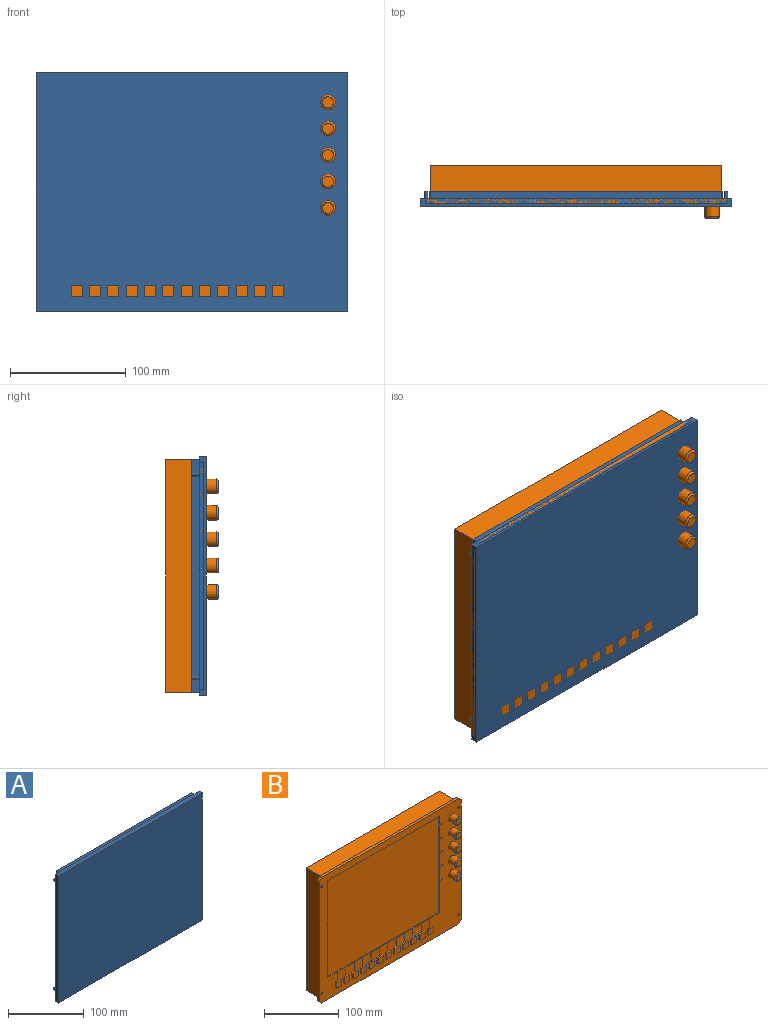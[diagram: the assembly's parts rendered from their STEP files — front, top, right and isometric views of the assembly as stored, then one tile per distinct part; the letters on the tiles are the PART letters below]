
ASSEMBLY  parts=2 mates=1
PART A: 19 faces, bbox 269.5x12.7x206 mm
  f0: plane 269.5x206mm, normal (0,1,0), area 4277.8mm2, adj f1,f2,f3,f4,f6,f7,f8,f9
  f1: plane 206x6.35mm, normal (1,0,0), area 1308.1mm2, adj f0,f2,f4,f5
  f2: plane 269.5x6.35mm, normal (0,0,1), area 1711.3mm2, adj f0,f1,f3,f5
  f3: plane 206x6.35mm, normal (-1,0,0), area 1308.1mm2, adj f0,f2,f4,f5
  f4: plane 269.5x6.35mm, normal (0,0,-1), area 1711.3mm2, adj f0,f1,f3,f5
  f5: plane 269.5x206mm, normal (0,-1,0), area 55517mm2, adj f1,f2,f3,f4
  f6: plane 253.5x6.35mm, normal (0,0,1), area 1609.7mm2, adj f0,f7,f9,f10
  f7: plane 202x6.35mm, normal (-1,0,0), area 1282.7mm2, adj f0,f6,f8,f10
  f8: plane 253.5x6.35mm, normal (0,0,-1), area 1609.7mm2, adj f0,f7,f9,f10
  f9: plane 202x6.35mm, normal (1,0,0), area 1282.7mm2, adj f0,f6,f8,f10
  f10: plane 253.5x202mm, normal (0,1,0), area 51207mm2, adj f6,f7,f8,f9
  f11: cylinder r=1.6mm len=6.35mm, axis (0,-1,0), area 63.8mm2, adj f0,f12
  f12: plane 3.2x3.2mm, normal (0,1,0), area 8mm2, adj f11
  f13: cylinder r=1.6mm len=6.35mm, axis (0,-1,0), area 63.8mm2, adj f0,f14
  f14: plane 3.2x3.2mm, normal (0,1,0), area 8mm2, adj f13
  f15: cylinder r=1.6mm len=6.35mm, axis (0,-1,0), area 63.8mm2, adj f0,f16
  f16: plane 3.2x3.2mm, normal (0,1,0), area 8mm2, adj f15
  f17: cylinder r=1.6mm len=6.35mm, axis (0,-1,0), area 63.8mm2, adj f0,f18
  f18: plane 3.2x3.2mm, normal (0,1,0), area 8mm2, adj f17
PART B: 219 faces, bbox 269.5x45.7x206 mm
  f0: plane 14.54x0.51mm, normal (1,0,0), area 7.4mm2, adj f2,f5,f88,f89
  f1: plane 14.54x0.51mm, normal (-1,0,0), area 7.4mm2, adj f2,f5,f88,f89
  f2: plane 14.54x0.25mm, normal (0,-1,0), area 3.7mm2, adj f0,f1,f5,f88
  f3: plane 9.53x2.54mm, normal (0,0,-1), area 24.2mm2, adj f4,f6,f7,f89
  f4: plane 9.53x2.54mm, normal (1,0,0), area 24.2mm2, adj f3,f5,f7,f89
  f5: plane 9.53x3.05mm, normal (0,0,1), area 24.3mm2, adj f0,f1,f2,f4,f6,f7,f89
  f6: plane 9.53x2.54mm, normal (-1,0,0), area 24.2mm2, adj f3,f5,f7,f89
  f7: plane 9.53x9.53mm, normal (0,-1,0), area 90.7mm2, adj f3,f4,f5,f6
  f8: plane 14.54x0.51mm, normal (1,0,0), area 7.4mm2, adj f10,f13,f88,f89
  f9: plane 14.54x0.51mm, normal (-1,0,0), area 7.4mm2, adj f10,f13,f88,f89
  f10: plane 14.54x0.25mm, normal (0,-1,0), area 3.7mm2, adj f8,f9,f13,f88
  f11: plane 9.53x2.54mm, normal (0,0,-1), area 24.2mm2, adj f12,f14,f15,f89
  f12: plane 9.53x2.54mm, normal (1,0,0), area 24.2mm2, adj f11,f13,f15,f89
  f13: plane 9.53x3.05mm, normal (0,0,1), area 24.3mm2, adj f8,f9,f10,f12,f14,f15,f89
  f14: plane 9.53x2.54mm, normal (-1,0,0), area 24.2mm2, adj f11,f13,f15,f89
  f15: plane 9.53x9.53mm, normal (0,-1,0), area 90.7mm2, adj f11,f12,f13,f14
  f16: plane 14.54x0.51mm, normal (1,0,0), area 7.4mm2, adj f18,f21,f88,f89
  f17: plane 14.54x0.51mm, normal (-1,0,0), area 7.4mm2, adj f18,f21,f88,f89
  f18: plane 14.54x0.25mm, normal (0,-1,0), area 3.7mm2, adj f16,f17,f21,f88
  f19: plane 9.53x2.54mm, normal (0,0,-1), area 24.2mm2, adj f20,f22,f23,f89
  f20: plane 9.53x2.54mm, normal (1,0,0), area 24.2mm2, adj f19,f21,f23,f89
  f21: plane 9.53x3.05mm, normal (0,0,1), area 24.3mm2, adj f16,f17,f18,f20,f22,f23,f89
  f22: plane 9.53x2.54mm, normal (-1,0,0), area 24.2mm2, adj f19,f21,f23,f89
  f23: plane 9.53x9.53mm, normal (0,-1,0), area 90.7mm2, adj f19,f20,f21,f22
  f24: plane 14.54x0.51mm, normal (1,0,0), area 7.4mm2, adj f26,f29,f88,f89
  f25: plane 14.54x0.51mm, normal (-1,0,0), area 7.4mm2, adj f26,f29,f88,f89
  f26: plane 14.54x0.25mm, normal (0,-1,0), area 3.7mm2, adj f24,f25,f29,f88
  f27: plane 9.53x2.54mm, normal (0,0,-1), area 24.2mm2, adj f28,f30,f31,f89
  f28: plane 9.53x2.54mm, normal (1,0,0), area 24.2mm2, adj f27,f29,f31,f89
  f29: plane 9.53x3.05mm, normal (0,0,1), area 24.3mm2, adj f24,f25,f26,f28,f30,f31,f89
  f30: plane 9.53x2.54mm, normal (-1,0,0), area 24.2mm2, adj f27,f29,f31,f89
  f31: plane 9.53x9.53mm, normal (0,-1,0), area 90.7mm2, adj f27,f28,f29,f30
  f32: plane 14.54x0.51mm, normal (1,0,0), area 7.4mm2, adj f34,f37,f88,f89
  f33: plane 14.54x0.51mm, normal (-1,0,0), area 7.4mm2, adj f34,f37,f88,f89
  f34: plane 14.54x0.25mm, normal (0,-1,0), area 3.7mm2, adj f32,f33,f37,f88
  f35: plane 9.53x2.54mm, normal (0,0,-1), area 24.2mm2, adj f36,f38,f39,f89
  f36: plane 9.53x2.54mm, normal (1,0,0), area 24.2mm2, adj f35,f37,f39,f89
  f37: plane 9.53x3.05mm, normal (0,0,1), area 24.3mm2, adj f32,f33,f34,f36,f38,f39,f89
  f38: plane 9.53x2.54mm, normal (-1,0,0), area 24.2mm2, adj f35,f37,f39,f89
  f39: plane 9.53x9.53mm, normal (0,-1,0), area 90.7mm2, adj f35,f36,f37,f38
  f40: plane 14.54x0.51mm, normal (1,0,0), area 7.4mm2, adj f42,f45,f88,f89
  f41: plane 14.54x0.51mm, normal (-1,0,0), area 7.4mm2, adj f42,f45,f88,f89
  f42: plane 14.54x0.25mm, normal (0,-1,0), area 3.7mm2, adj f40,f41,f45,f88
  f43: plane 9.53x2.54mm, normal (0,0,-1), area 24.2mm2, adj f44,f46,f47,f89
  f44: plane 9.53x2.54mm, normal (1,0,0), area 24.2mm2, adj f43,f45,f47,f89
  f45: plane 9.53x3.05mm, normal (0,0,1), area 24.3mm2, adj f40,f41,f42,f44,f46,f47,f89
  f46: plane 9.53x2.54mm, normal (-1,0,0), area 24.2mm2, adj f43,f45,f47,f89
  f47: plane 9.53x9.53mm, normal (0,-1,0), area 90.7mm2, adj f43,f44,f45,f46
  f48: plane 14.54x0.51mm, normal (1,0,0), area 7.4mm2, adj f50,f53,f88,f89
  f49: plane 14.54x0.51mm, normal (-1,0,0), area 7.4mm2, adj f50,f53,f88,f89
  f50: plane 14.54x0.25mm, normal (0,-1,0), area 3.7mm2, adj f48,f49,f53,f88
  f51: plane 9.53x2.54mm, normal (0,0,-1), area 24.2mm2, adj f52,f54,f55,f89
  f52: plane 9.53x2.54mm, normal (1,0,0), area 24.2mm2, adj f51,f53,f55,f89
  f53: plane 9.53x3.05mm, normal (0,0,1), area 24.3mm2, adj f48,f49,f50,f52,f54,f55,f89
  f54: plane 9.53x2.54mm, normal (-1,0,0), area 24.2mm2, adj f51,f53,f55,f89
  f55: plane 9.53x9.53mm, normal (0,-1,0), area 90.7mm2, adj f51,f52,f53,f54
  f56: plane 14.54x0.51mm, normal (1,0,0), area 7.4mm2, adj f58,f61,f88,f89
  f57: plane 14.54x0.51mm, normal (-1,0,0), area 7.4mm2, adj f58,f61,f88,f89
  f58: plane 14.54x0.25mm, normal (0,-1,0), area 3.7mm2, adj f56,f57,f61,f88
  f59: plane 9.53x2.54mm, normal (0,0,-1), area 24.2mm2, adj f60,f62,f63,f89
  f60: plane 9.53x2.54mm, normal (1,0,0), area 24.2mm2, adj f59,f61,f63,f89
  f61: plane 9.53x3.05mm, normal (0,0,1), area 24.3mm2, adj f56,f57,f58,f60,f62,f63,f89
  f62: plane 9.53x2.54mm, normal (-1,0,0), area 24.2mm2, adj f59,f61,f63,f89
  f63: plane 9.53x9.53mm, normal (0,-1,0), area 90.7mm2, adj f59,f60,f61,f62
  f64: plane 14.54x0.51mm, normal (1,0,0), area 7.4mm2, adj f66,f69,f88,f89
  f65: plane 14.54x0.51mm, normal (-1,0,0), area 7.4mm2, adj f66,f69,f88,f89
  f66: plane 14.54x0.25mm, normal (0,-1,0), area 3.7mm2, adj f64,f65,f69,f88
  f67: plane 9.53x2.54mm, normal (0,0,-1), area 24.2mm2, adj f68,f70,f71,f89
  f68: plane 9.53x2.54mm, normal (1,0,0), area 24.2mm2, adj f67,f69,f71,f89
  f69: plane 9.53x3.05mm, normal (0,0,1), area 24.3mm2, adj f64,f65,f66,f68,f70,f71,f89
  f70: plane 9.53x2.54mm, normal (-1,0,0), area 24.2mm2, adj f67,f69,f71,f89
  f71: plane 9.53x9.53mm, normal (0,-1,0), area 90.7mm2, adj f67,f68,f69,f70
  f72: plane 14.54x0.51mm, normal (1,0,0), area 7.4mm2, adj f74,f77,f88,f89
  f73: plane 14.54x0.51mm, normal (-1,0,0), area 7.4mm2, adj f74,f77,f88,f89
  f74: plane 14.54x0.25mm, normal (0,-1,0), area 3.7mm2, adj f72,f73,f77,f88
  f75: plane 9.53x2.54mm, normal (0,0,-1), area 24.2mm2, adj f76,f78,f79,f89
  f76: plane 9.53x2.54mm, normal (1,0,0), area 24.2mm2, adj f75,f77,f79,f89
  f77: plane 9.53x3.05mm, normal (0,0,1), area 24.3mm2, adj f72,f73,f74,f76,f78,f79,f89
  f78: plane 9.53x2.54mm, normal (-1,0,0), area 24.2mm2, adj f75,f77,f79,f89
  f79: plane 9.53x9.53mm, normal (0,-1,0), area 90.7mm2, adj f75,f76,f77,f78
  f80: plane 14.54x0.51mm, normal (1,0,0), area 7.4mm2, adj f82,f85,f88,f89
  f81: plane 14.54x0.51mm, normal (-1,0,0), area 7.4mm2, adj f82,f85,f88,f89
  f82: plane 14.54x0.25mm, normal (0,-1,0), area 3.7mm2, adj f80,f81,f85,f88
  f83: plane 9.53x2.54mm, normal (0,0,-1), area 24.2mm2, adj f84,f86,f87,f89
  f84: plane 9.53x2.54mm, normal (1,0,0), area 24.2mm2, adj f83,f85,f87,f89
  f85: plane 9.53x3.05mm, normal (0,0,1), area 24.3mm2, adj f80,f81,f82,f84,f86,f87,f89
  f86: plane 9.53x2.54mm, normal (-1,0,0), area 24.2mm2, adj f83,f85,f87,f89
  f87: plane 9.53x9.53mm, normal (0,-1,0), area 90.7mm2, adj f83,f84,f85,f86
  f88: plane 211.33x1.59mm, normal (0,0,1), area 333.9mm2, adj f0,f1,f2,f8,f9,f10,f16,f17
  f89: plane 269.5x206mm, normal (0,-1,0), area 20165.7mm2, adj f0,f1,f3,f4,f5,f6,f8,f9
  f90: cylinder r=1.59mm len=6.35mm, axis (0,1,0), area 63.3mm2, adj f91,f169
  f91: plane 3.18x3.18mm, normal (0,1,0), area 7.9mm2, adj f90
  f92: cylinder r=1.59mm len=6.35mm, axis (0,1,0), area 63.3mm2, adj f93,f169
  f93: plane 3.18x3.18mm, normal (0,1,0), area 7.9mm2, adj f92
  f94: cylinder r=1.59mm len=6.35mm, axis (0,1,0), area 63.3mm2, adj f95,f169
  f95: plane 3.18x3.18mm, normal (0,1,0), area 7.9mm2, adj f94
  f96: cylinder r=1.59mm len=6.35mm, axis (0,1,0), area 63.3mm2, adj f97,f169
  f97: plane 3.18x3.18mm, normal (0,1,0), area 7.9mm2, adj f96
  f98: cylinder r=1.59mm len=6.35mm, axis (0,1,0), area 63.3mm2, adj f99,f169
  f99: plane 3.18x3.18mm, normal (0,1,0), area 7.9mm2, adj f98
  f100: cylinder r=1.59mm len=6.35mm, axis (0,1,0), area 63.3mm2, adj f101,f169
  f101: plane 3.18x3.18mm, normal (0,1,0), area 7.9mm2, adj f100
  f102: cylinder r=1.59mm len=6.35mm, axis (0,1,0), area 63.3mm2, adj f103,f169
  f103: plane 3.18x3.18mm, normal (0,1,0), area 7.9mm2, adj f102
  f104: cylinder r=1.59mm len=6.35mm, axis (0,1,0), area 63.3mm2, adj f105,f169
  f105: plane 3.18x3.18mm, normal (0,1,0), area 7.9mm2, adj f104
  f106: cylinder r=1.59mm len=6.35mm, axis (0,1,0), area 63.3mm2, adj f107,f169
  f107: plane 3.18x3.18mm, normal (0,1,0), area 7.9mm2, adj f106
  f108: cylinder r=1.59mm len=6.35mm, axis (0,1,0), area 63.3mm2, adj f109,f169
  f109: plane 3.18x3.18mm, normal (0,1,0), area 7.9mm2, adj f108
  f110: cylinder r=1.59mm len=6.35mm, axis (0,1,0), area 63.3mm2, adj f111,f169
  f111: plane 3.18x3.18mm, normal (0,1,0), area 7.9mm2, adj f110
  f112: cylinder r=1.59mm len=6.35mm, axis (0,1,0), area 63.3mm2, adj f113,f169
  f113: plane 3.18x3.18mm, normal (0,1,0), area 7.9mm2, adj f112
  f114: cylinder r=1.59mm len=6.35mm, axis (0,1,0), area 63.3mm2, adj f115,f169
  f115: plane 3.18x3.18mm, normal (0,1,0), area 7.9mm2, adj f114
  f116: cylinder r=1.59mm len=6.35mm, axis (0,1,0), area 63.3mm2, adj f117,f169
  f117: plane 3.18x3.18mm, normal (0,1,0), area 7.9mm2, adj f116
  f118: cylinder r=1.59mm len=6.35mm, axis (0,1,0), area 63.3mm2, adj f119,f169
  f119: plane 3.18x3.18mm, normal (0,1,0), area 7.9mm2, adj f118
  f120: cylinder r=1.59mm len=6.35mm, axis (0,1,0), area 63.3mm2, adj f121,f169
  f121: plane 3.18x3.18mm, normal (0,1,0), area 7.9mm2, adj f120
  f122: cylinder r=1.59mm len=6.35mm, axis (0,1,0), area 63.3mm2, adj f123,f169
  f123: plane 3.18x3.18mm, normal (0,1,0), area 7.9mm2, adj f122
  f124: cylinder r=1.59mm len=6.35mm, axis (0,1,0), area 63.3mm2, adj f125,f169
  f125: plane 3.18x3.18mm, normal (0,1,0), area 7.9mm2, adj f124
  f126: cylinder r=1.59mm len=6.35mm, axis (0,1,0), area 63.3mm2, adj f127,f169
  f127: plane 3.18x3.18mm, normal (0,1,0), area 7.9mm2, adj f126
  f128: cylinder r=1.59mm len=6.35mm, axis (0,1,0), area 63.3mm2, adj f129,f169
  f129: plane 3.18x3.18mm, normal (0,1,0), area 7.9mm2, adj f128
  f130: cylinder r=1.59mm len=6.35mm, axis (0,1,0), area 63.3mm2, adj f131,f169
  f131: plane 3.18x3.18mm, normal (0,1,0), area 7.9mm2, adj f130
  f132: cylinder r=1.59mm len=6.35mm, axis (0,1,0), area 63.3mm2, adj f133,f169
  f133: plane 3.18x3.18mm, normal (0,1,0), area 7.9mm2, adj f132
  f134: cylinder r=1.59mm len=6.35mm, axis (0,1,0), area 63.3mm2, adj f135,f169
  f135: plane 3.18x3.18mm, normal (0,1,0), area 7.9mm2, adj f134
  f136: cylinder r=1.59mm len=6.35mm, axis (0,1,0), area 63.3mm2, adj f137,f169
  f137: plane 3.18x3.18mm, normal (0,1,0), area 7.9mm2, adj f136
  f138: cylinder r=1.59mm len=6.35mm, axis (0,1,0), area 63.3mm2, adj f139,f169
  f139: plane 3.18x3.18mm, normal (0,1,0), area 7.9mm2, adj f138
  f140: cylinder r=1.59mm len=6.35mm, axis (0,1,0), area 63.3mm2, adj f141,f169
  f141: plane 3.18x3.18mm, normal (0,1,0), area 7.9mm2, adj f140
  f142: cylinder r=1.59mm len=6.35mm, axis (0,1,0), area 63.3mm2, adj f143,f169
  f143: plane 3.18x3.18mm, normal (0,1,0), area 7.9mm2, adj f142
  f144: cylinder r=1.59mm len=6.35mm, axis (0,1,0), area 63.3mm2, adj f145,f169
  f145: plane 3.18x3.18mm, normal (0,1,0), area 7.9mm2, adj f144
  f146: cylinder r=1.59mm len=6.35mm, axis (0,1,0), area 63.3mm2, adj f147,f169
  f147: plane 3.18x3.18mm, normal (0,1,0), area 7.9mm2, adj f146
  f148: cylinder r=1.59mm len=6.35mm, axis (0,1,0), area 63.3mm2, adj f149,f169
  f149: plane 3.18x3.18mm, normal (0,1,0), area 7.9mm2, adj f148
  f150: cylinder r=1.59mm len=6.35mm, axis (0,1,0), area 63.3mm2, adj f151,f169
  f151: plane 3.18x3.18mm, normal (0,1,0), area 7.9mm2, adj f150
  f152: plane 196x4mm, normal (1,0,0), area 784mm2, adj f89,f160,f162,f163
  f153: plane 259.5x4mm, normal (0,0,1), area 1038mm2, adj f89,f160,f163,f164
  f154: plane 196x4mm, normal (-1,0,0), area 784mm2, adj f89,f160,f161,f164
  f155: cylinder r=1.6mm len=4mm, axis (0,1,0), area 40.2mm2, adj f89,f160
  f156: cylinder r=1.6mm len=4mm, axis (0,1,0), area 40.2mm2, adj f89,f160
  f157: cylinder r=1.6mm len=4mm, axis (0,1,0), area 40.2mm2, adj f89,f160
  f158: plane 259.5x4mm, normal (0,0,-1), area 1038mm2, adj f89,f160,f161,f162
  f159: cylinder r=1.6mm len=4mm, axis (0,1,0), area 40.2mm2, adj f89,f160
  f160: plane 269.5x206mm, normal (0,1,0), area 4682.3mm2, adj f152,f153,f154,f155,f156,f157,f158,f159
  f161: plane 5x5mm, normal (-0.71,0,-0.71), area 28.3mm2, adj f89,f154,f158,f160
  f162: plane 5x5mm, normal (0.71,0,-0.71), area 28.3mm2, adj f89,f152,f158,f160
  f163: plane 5x5mm, normal (0.71,0,0.71), area 28.3mm2, adj f89,f152,f153,f160
  f164: plane 5x5mm, normal (-0.71,0,0.71), area 28.3mm2, adj f89,f153,f154,f160
  f165: plane 252.5x29mm, normal (0,0,-1), area 7322.5mm2, adj f160,f166,f168,f169
  f166: plane 201x29mm, normal (-1,0,0), area 5829mm2, adj f160,f165,f167,f169
  f167: plane 252.5x29mm, normal (0,0,1), area 7322.5mm2, adj f160,f166,f168,f169
  f168: plane 201x29mm, normal (1,0,0), area 5829mm2, adj f160,f165,f167,f169
  f169: plane 252.5x201mm, normal (0,1,0), area 50499.1mm2, adj f90,f92,f94,f96,f98,f100,f102,f104
  f170: cylinder r=1.59mm len=6.35mm, axis (0,1,0), area 63.3mm2, adj f169,f171
  f171: plane 3.18x3.18mm, normal (0,1,0), area 7.9mm2, adj f170
  f172: plane 158.5x2.1mm, normal (-1,0,0), area 252.3mm2, adj f88,f89,f173,f175,f179,f180,f182,f186
  f173: plane 211.33x1.59mm, normal (0,0,-1), area 335.5mm2, adj f89,f172,f174,f175
  f174: plane 158.5x1.59mm, normal (1,0,0), area 251.6mm2, adj f88,f89,f173,f175
  f175: plane 211.33x158.5mm, normal (0,-1,0), area 33494.6mm2, adj f88,f172,f173,f174
  f176: cylinder r=6.35mm len=12.7mm, axis (0,1,0), area 443.4mm2, adj f89,f178
  f177: plane 9.53x9.53mm, normal (0,-1,0), area 71.3mm2, adj f178
  f178: torus R=4.76mm, axis (0,-1,0), area 90.5mm2, adj f176,f177
  f179: plane 6.35x0.51mm, normal (0,0,1), area 3.2mm2, adj f89,f172,f181,f182
  f180: plane 6.35x0.51mm, normal (0,0,-1), area 3.2mm2, adj f89,f172,f181,f182
  f181: plane 0.51x0.25mm, normal (1,0,0), area 0.1mm2, adj f89,f179,f180,f182
  f182: plane 6.35x0.25mm, normal (0,-1,0), area 1.6mm2, adj f172,f179,f180,f181
  f183: cylinder r=6.35mm len=12.7mm, axis (0,1,0), area 443.4mm2, adj f89,f185
  f184: plane 9.53x9.53mm, normal (0,-1,0), area 71.3mm2, adj f185
  f185: torus R=4.76mm, axis (0,-1,0), area 90.5mm2, adj f183,f184
  f186: plane 6.35x0.51mm, normal (0,0,1), area 3.2mm2, adj f89,f172,f188,f189
  f187: plane 6.35x0.51mm, normal (0,0,-1), area 3.2mm2, adj f89,f172,f188,f189
  f188: plane 0.51x0.25mm, normal (1,0,0), area 0.1mm2, adj f89,f186,f187,f189
  f189: plane 6.35x0.25mm, normal (0,-1,0), area 1.6mm2, adj f172,f186,f187,f188
  f190: cylinder r=6.35mm len=12.7mm, axis (0,1,0), area 443.4mm2, adj f89,f192
  f191: plane 9.53x9.53mm, normal (0,-1,0), area 71.3mm2, adj f192
  f192: torus R=4.76mm, axis (0,-1,0), area 90.5mm2, adj f190,f191
  f193: plane 6.35x0.51mm, normal (0,0,1), area 3.2mm2, adj f89,f172,f195,f196
  f194: plane 6.35x0.51mm, normal (0,0,-1), area 3.2mm2, adj f89,f172,f195,f196
  f195: plane 0.51x0.25mm, normal (1,0,0), area 0.1mm2, adj f89,f193,f194,f196
  f196: plane 6.35x0.25mm, normal (0,-1,0), area 1.6mm2, adj f172,f193,f194,f195
  f197: cylinder r=6.35mm len=12.7mm, axis (0,1,0), area 443.4mm2, adj f89,f199
  f198: plane 9.53x9.53mm, normal (0,-1,0), area 71.3mm2, adj f199
  f199: torus R=4.76mm, axis (0,-1,0), area 90.5mm2, adj f197,f198
  f200: plane 6.35x0.51mm, normal (0,0,1), area 3.2mm2, adj f89,f172,f202,f203
  f201: plane 6.35x0.51mm, normal (0,0,-1), area 3.2mm2, adj f89,f172,f202,f203
  f202: plane 0.51x0.25mm, normal (1,0,0), area 0.1mm2, adj f89,f200,f201,f203
  f203: plane 6.35x0.25mm, normal (0,-1,0), area 1.6mm2, adj f172,f200,f201,f202
  f204: cylinder r=6.35mm len=12.7mm, axis (0,1,0), area 443.4mm2, adj f89,f206
  f205: plane 9.53x9.53mm, normal (0,-1,0), area 71.3mm2, adj f206
  f206: torus R=4.76mm, axis (0,-1,0), area 90.5mm2, adj f204,f205
  f207: plane 6.35x0.51mm, normal (0,0,1), area 3.2mm2, adj f89,f172,f209,f210
  f208: plane 6.35x0.51mm, normal (0,0,-1), area 3.2mm2, adj f89,f172,f209,f210
  f209: plane 0.51x0.25mm, normal (1,0,0), area 0.1mm2, adj f89,f207,f208,f210
  f210: plane 6.35x0.25mm, normal (0,-1,0), area 1.6mm2, adj f172,f207,f208,f209
  f211: plane 9.53x2.54mm, normal (0,0,-1), area 24.2mm2, adj f89,f212,f214,f215
  f212: plane 9.53x2.54mm, normal (1,0,0), area 24.2mm2, adj f89,f211,f213,f215
  f213: plane 9.53x3.05mm, normal (0,0,1), area 24.3mm2, adj f89,f212,f214,f215,f216,f217,f218
  f214: plane 9.53x2.54mm, normal (-1,0,0), area 24.2mm2, adj f89,f211,f213,f215
  f215: plane 9.53x9.53mm, normal (0,-1,0), area 90.7mm2, adj f211,f212,f213,f214
  f216: plane 14.54x0.51mm, normal (1,0,0), area 7.4mm2, adj f88,f89,f213,f218
  f217: plane 14.54x0.51mm, normal (-1,0,0), area 7.4mm2, adj f88,f89,f213,f218
  f218: plane 14.54x0.25mm, normal (0,-1,0), area 3.7mm2, adj f88,f213,f216,f217
PLACE A at identity
PLACE B at identity fixed
MATE fastened B.f160 <-> A.f0  axis (0,-1,0) through (0,0,0)mm
